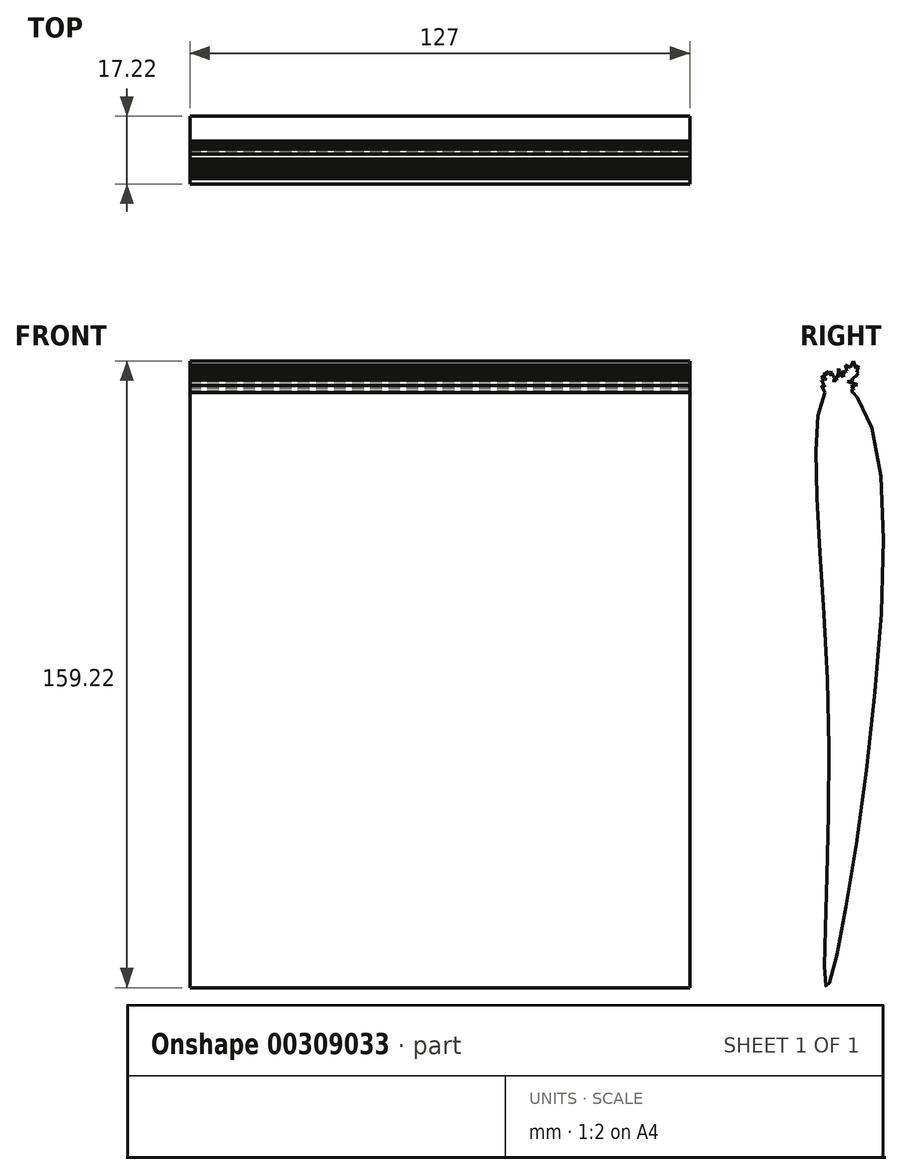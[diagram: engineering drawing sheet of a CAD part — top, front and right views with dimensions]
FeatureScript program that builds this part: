
annotation { "Feature Type Name" : "Feature", "Feature Type Description" : "" }
export const myFeature = defineFeature(function(context is Context, id is Id, definition is map)
    precondition{}
    {
        {
            var Q0;
            Q0=qCreatedBy(makeId("Right.planeOp"),FACE);
            var sketch = newSketch(context, id + "F0", { "sketchPlane" : qUnion([Q0])});
            skFitSpline(sketch, "E0", {"points": [v(-2.03, 75.34) * mm, v(9.75, 62.3) * mm, v(-2.03, -76.46) * mm, v(-2.03, -8.77) * mm, v(-2.03, 75.34) * mm]});
            skLineSegment(sketch, "E1", {"start": v(0.74, 76.19) * mm, "end": v(3, 80.27) * mm});
            skLineSegment(sketch, "E2", {"start": v(3, 80.27) * mm, "end": v(4.24, 79.58) * mm});
            skLineSegment(sketch, "E3", {"start": v(4.24, 79.58) * mm, "end": v(2.09, 75.7) * mm});
            skLineSegment(sketch, "E4", {"start": v(2.09, 75.7) * mm, "end": v(0.74, 76.19) * mm});
            skLineSegment(sketch, "E5", {"start": v(-0.38, 76.14) * mm, "end": v(-1.65, 78.86) * mm});
            skLineSegment(sketch, "E6", {"start": v(-1.65, 78.86) * mm, "end": v(-2.8, 78.32) * mm});
            skLineSegment(sketch, "E7", {"start": v(-2.8, 78.32) * mm, "end": v(-1.59, 75.67) * mm});
            skLineSegment(sketch, "E8", {"start": v(-1.59, 75.67) * mm, "end": v(-0.38, 76.14) * mm});
            skLineSegment(sketch, "E9", {"start": v(3.68, 74.6) * mm, "end": v(3.68, 76.14) * mm});
            skLineSegment(sketch, "E10", {"start": v(3.68, 76.14) * mm, "end": v(2.09, 75.7) * mm});
            skLineSegment(sketch, "E11", {"start": v(3.16, 77.64) * mm, "end": v(4.3, 77.02) * mm});
            skLineSegment(sketch, "E12", {"start": v(4.3, 77.02) * mm, "end": v(2.81, 77.02) * mm});
            skLineSegment(sketch, "E13", {"start": v(2.81, 77.02) * mm, "end": v(5.28, 76.24) * mm});
            skLineSegment(sketch, "E14", {"start": v(5.28, 76.24) * mm, "end": v(3.68, 75.7) * mm});
            skLineSegment(sketch, "E15", {"start": v(3.68, 75.7) * mm, "end": v(4.56, 75.21) * mm});
            skLineSegment(sketch, "E16", {"start": v(4.56, 75.21) * mm, "end": v(3.68, 74.6) * mm});
            skLineSegment(sketch, "E17", {"start": v(4.06, 79.26) * mm, "end": v(5.61, 77.98) * mm});
            skLineSegment(sketch, "E18", {"start": v(5.61, 77.98) * mm, "end": v(3.73, 77.33) * mm});
            skLineSegment(sketch, "E19", {"start": v(3.73, 77.33) * mm, "end": v(5.61, 79.02) * mm});
            skLineSegment(sketch, "E20", {"start": v(5.61, 79.02) * mm, "end": v(4.24, 79.58) * mm});
            skLineSegment(sketch, "E21", {"start": v(5.2, 79.19) * mm, "end": v(5.61, 80.99) * mm});
            skLineSegment(sketch, "E22", {"start": v(5.61, 80.99) * mm, "end": v(4.24, 79.58) * mm});
            skLineSegment(sketch, "E23", {"start": v(4.93, 80.29) * mm, "end": v(4.24, 82.18) * mm});
            skLineSegment(sketch, "E24", {"start": v(4.24, 82.18) * mm, "end": v(3.53, 80.45) * mm});
            skLineSegment(sketch, "E25", {"start": v(3.53, 80.45) * mm, "end": v(2.25, 81.17) * mm});
            skLineSegment(sketch, "E26", {"start": v(2.25, 81.17) * mm, "end": v(2.62, 79.58) * mm});
            skLineSegment(sketch, "E27", {"start": v(2.62, 79.58) * mm, "end": v(0.99, 79.2) * mm});
            skLineSegment(sketch, "E28", {"start": v(0.99, 79.2) * mm, "end": v(2.07, 78.6) * mm});
            skLineSegment(sketch, "E29", {"start": v(2.07, 78.6) * mm, "end": v(0.38, 78.02) * mm});
            skLineSegment(sketch, "E30", {"start": v(0.38, 78.02) * mm, "end": v(0.42, 80.28) * mm});
            skLineSegment(sketch, "E31", {"start": v(0.42, 80.28) * mm, "end": v(1.1, 78.27) * mm});
            skLineSegment(sketch, "E32", {"start": v(1.1, 78.27) * mm, "end": v(2.07, 78.6) * mm});
            skLineSegment(sketch, "E33", {"start": v(0.38, 78.02) * mm, "end": v(-0.23, 78.27) * mm});
            skLineSegment(sketch, "E34", {"start": v(-0.23, 78.27) * mm, "end": v(0.14, 77.19) * mm});
            skLineSegment(sketch, "E35", {"start": v(0.14, 77.19) * mm, "end": v(-0.43, 77.42) * mm});
            skLineSegment(sketch, "E36", {"start": v(-0.43, 77.42) * mm, "end": v(-0.69, 76.8) * mm});
            skLineSegment(sketch, "E37", {"start": v(-0.69, 76.8) * mm, "end": v(-0.58, 78.35) * mm});
            skLineSegment(sketch, "E38", {"start": v(-0.58, 78.35) * mm, "end": v(-1.44, 78.41) * mm});
            skLineSegment(sketch, "E39", {"start": v(-1.44, 78.41) * mm, "end": v(-1.44, 79.58) * mm});
            skLineSegment(sketch, "E40", {"start": v(-1.44, 79.58) * mm, "end": v(-1.84, 78.86) * mm});
            skLineSegment(sketch, "E41", {"start": v(-1.84, 78.86) * mm, "end": v(-2.58, 79.58) * mm});
            skLineSegment(sketch, "E42", {"start": v(-2.58, 79.58) * mm, "end": v(-2.15, 78.32) * mm});
            skLineSegment(sketch, "E43", {"start": v(-2.15, 78.32) * mm, "end": v(-3.46, 78.86) * mm});
            skLineSegment(sketch, "E44", {"start": v(-3.46, 78.86) * mm, "end": v(-2.33, 78.86) * mm});
            skLineSegment(sketch, "E45", {"start": v(-2.33, 78.86) * mm, "end": v(-3.96, 78.02) * mm});
            skLineSegment(sketch, "E46", {"start": v(-3.96, 78.02) * mm, "end": v(-2.67, 78.02) * mm});
            skLineSegment(sketch, "E47", {"start": v(-2.67, 78.02) * mm, "end": v(-3.4, 76.68) * mm});
            skLineSegment(sketch, "E48", {"start": v(-3.4, 76.68) * mm, "end": v(-2.2, 77.24) * mm});
            skPoint(sketch, "E48.endSnap0", {"position": v(-2.2, 77) * mm});
            skLineSegment(sketch, "E49", {"start": v(-2.2, 77.24) * mm, "end": v(-2.8, 76.05) * mm});
            skLineSegment(sketch, "E50", {"start": v(-2.8, 76.05) * mm, "end": v(-1.59, 75.67) * mm});
            skLineSegment(sketch, "E51", {"start": v(-2.5, 74.85) * mm, "end": v(-3.39, 75.34) * mm});
            skPoint(sketch, "E51.startSnap0", {"position": v(-2.5, 76.65) * mm});
            skLineSegment(sketch, "E52", {"start": v(-3.39, 75.34) * mm, "end": v(-2.03, 76.05) * mm});
            skLineSegment(sketch, "E53", {"start": v(-3.04, 77.35) * mm, "end": v(-3.85, 77.35) * mm});
            skLineSegment(sketch, "E54", {"start": v(-3.85, 77.35) * mm, "end": v(-3, 75.54) * mm});
            skLineSegment(sketch, "E55", {"start": v(-3, 75.54) * mm, "end": v(-3.82, 75.98) * mm});
            skLineSegment(sketch, "E56", {"start": v(-3.82, 75.98) * mm, "end": v(-2.98, 74.17) * mm});
            skLineSegment(sketch, "E57", {"start": v(-2.98, 74.17) * mm, "end": v(-2.5, 74.85) * mm});
            skLineSegment(sketch, "E58", {"start": v(-1.01, 78.35) * mm, "end": v(-1.01, 79.15) * mm});
            skPoint(sketch, "E58.startSnap0", {"position": v(-1.01, 78.38) * mm});
            skPoint(sketch, "E58.endSnap0", {"position": v(0.4, 79.15) * mm});
            skLineSegment(sketch, "E59", {"start": v(-1.01, 79.15) * mm, "end": v(-1.44, 78.41) * mm});
            skLineSegment(sketch, "E60", {"start": v(4.56, 73.73) * mm, "end": v(5.43, 75.21) * mm});
            skLineSegment(sketch, "E61", {"start": v(5.43, 75.21) * mm, "end": v(4.12, 74.2) * mm});
            skPoint(sketch, "E61.endSnap0", {"position": v(4.12, 74.91) * mm});
            skLineSegment(sketch, "E62", {"start": v(4.12, 74.2) * mm, "end": v(5.28, 76.24) * mm});
            skLineSegment(sketch, "E63", {"start": v(5.43, 75.21) * mm, "end": v(5.28, 76.24) * mm});
            skLineSegment(sketch, "E64", {"start": v(5, 74.47) * mm, "end": v(5.43, 74.22) * mm});
            skLineSegment(sketch, "E65", {"start": v(5.43, 74.22) * mm, "end": v(5.28, 73.96) * mm});
            skLineSegment(sketch, "E66", {"start": v(5.28, 73.96) * mm, "end": v(5.28, 72.85) * mm});
            skLineSegment(sketch, "E67", {"start": v(5.28, 72.85) * mm, "end": v(5.43, 74.22) * mm});
            skLineSegment(sketch, "E68", {"start": v(5, 74.47) * mm, "end": v(5.43, 74.77) * mm});
            skLineSegment(sketch, "E69", {"start": v(5.43, 74.77) * mm, "end": v(5.43, 74.22) * mm});
            skLineSegment(sketch, "E70", {"start": v(5.43, 75.21) * mm, "end": v(6.01, 76.24) * mm});
            skLineSegment(sketch, "E71", {"start": v(6.01, 76.24) * mm, "end": v(5.28, 76.24) * mm});
            skLineSegment(sketch, "E72", {"start": v(5.43, 75.21) * mm, "end": v(6.04, 75.64) * mm});
            skLineSegment(sketch, "E73", {"start": v(6.04, 75.64) * mm, "end": v(5.73, 75.6) * mm});
            skPoint(sketch, "E73.endSnap0", {"position": v(5.73, 75.43) * mm});
            skLineSegment(sketch, "E74", {"start": v(5.73, 75.6) * mm, "end": v(5.43, 75.21) * mm});
            skLineSegment(sketch, "E75", {"start": v(5.28, 76.24) * mm, "end": v(5.02, 77.02) * mm});
            skPoint(sketch, "E75.endSnap0", {"position": v(3.55, 77.02) * mm});
            skLineSegment(sketch, "E76", {"start": v(5.02, 77.02) * mm, "end": v(4.33, 76.54) * mm});
            skLineSegment(sketch, "E77", {"start": v(4.33, 76.54) * mm, "end": v(4.57, 77.33) * mm});
            skLineSegment(sketch, "E78", {"start": v(4.57, 77.33) * mm, "end": v(4.3, 77.02) * mm});
            skLineSegment(sketch, "E79", {"start": v(6.01, 76.24) * mm, "end": v(5.73, 76.64) * mm});
            skLineSegment(sketch, "E80", {"start": v(5.73, 76.64) * mm, "end": v(5.28, 76.24) * mm});
            skLineSegment(sketch, "E81", {"start": v(5.15, 76.63) * mm, "end": v(5.28, 76.86) * mm});
            skLineSegment(sketch, "E82", {"start": v(5.28, 76.86) * mm, "end": v(5.28, 76.24) * mm});
            skLineSegment(sketch, "E83", {"start": v(4.67, 76.78) * mm, "end": v(4.64, 77.02) * mm});
            skLineSegment(sketch, "E84", {"start": v(4.64, 77.02) * mm, "end": v(4.3, 77.02) * mm});
            skLineSegment(sketch, "E85", {"start": v(5.87, 76.44) * mm, "end": v(5.87, 77.02) * mm});
            skLineSegment(sketch, "E86", {"start": v(5.87, 77.02) * mm, "end": v(5.28, 76.5) * mm});
            skLineSegment(sketch, "E87", {"start": v(5.28, 76.5) * mm, "end": v(5.44, 77.02) * mm});
            skLineSegment(sketch, "E88", {"start": v(5.44, 77.02) * mm, "end": v(5.28, 76.86) * mm});
            skLineSegment(sketch, "E89", {"start": v(5.02, 77.02) * mm, "end": v(5.28, 77.25) * mm});
            skLineSegment(sketch, "E90", {"start": v(5.28, 77.25) * mm, "end": v(5.28, 76.86) * mm});
            skLineSegment(sketch, "E91", {"start": v(5.02, 77.02) * mm, "end": v(4.91, 77.33) * mm});
            skLineSegment(sketch, "E92", {"start": v(4.91, 77.33) * mm, "end": v(4.64, 77.02) * mm});
            skLineSegment(sketch, "E93", {"start": v(3.73, 77.33) * mm, "end": v(4.3, 77.41) * mm});
            skLineSegment(sketch, "E94", {"start": v(4.3, 77.41) * mm, "end": v(4.3, 77.02) * mm});
            skLineSegment(sketch, "E95", {"start": v(5.61, 77.98) * mm, "end": v(5.73, 78.37) * mm});
            skLineSegment(sketch, "E96", {"start": v(5.73, 78.37) * mm, "end": v(5.49, 78.09) * mm});
            skLineSegment(sketch, "E97", {"start": v(5.49, 78.09) * mm, "end": v(5.45, 78.6) * mm});
            skLineSegment(sketch, "E98", {"start": v(5.45, 78.6) * mm, "end": v(5.17, 78.35) * mm});
            skLineSegment(sketch, "E99", {"start": v(5.17, 78.35) * mm, "end": v(5.61, 79.02) * mm});
            skLineSegment(sketch, "E100", {"start": v(3.24, 77.37) * mm, "end": v(4.91, 77.33) * mm});
            skPoint(sketch, "E100.startSnap0", {"position": v(4.01, 77.37) * mm});
            skLineSegment(sketch, "E101", {"start": v(4.91, 77.33) * mm, "end": v(5.61, 77.98) * mm});
            skLineSegment(sketch, "E102", {"start": v(5.61, 79.02) * mm, "end": v(5.73, 79.88) * mm});
            skLineSegment(sketch, "E103", {"start": v(5.73, 79.88) * mm, "end": v(5.2, 79.19) * mm});
            skLineSegment(sketch, "E104", {"start": v(5.47, 79.54) * mm, "end": v(5.64, 80.29) * mm});
            skLineSegment(sketch, "E105", {"start": v(5.64, 80.29) * mm, "end": v(5.4, 80) * mm});
            skPoint(sketch, "E105.endSnap0", {"position": v(5.4, 80.09) * mm});
            skLineSegment(sketch, "E106", {"start": v(5.4, 80) * mm, "end": v(5.2, 79.19) * mm});
            skLineSegment(sketch, "E107", {"start": v(4.67, 80.98) * mm, "end": v(5.02, 81.43) * mm});
            skLineSegment(sketch, "E108", {"start": v(5.02, 81.43) * mm, "end": v(4.93, 80.29) * mm});
            skLineSegment(sketch, "E109", {"start": v(4.99, 80.82) * mm, "end": v(5.28, 80.82) * mm});
            skLineSegment(sketch, "E110", {"start": v(5.28, 80.82) * mm, "end": v(5.3, 80.66) * mm});
            skSolve(sketch);
        }
        {
            var Q0;
            {var subQ6=sQuery(id+"F0.wireOp",EDGE,"E8");Q0=makeQuery(id+"F0.imprint","IMPRINT",FACE,{"disambiguationData":[TD([[makeQuery(id+"F0.imprint","IMPRINT",EDGE,{"derivedFrom":subQ6}),-1.0]])]});}
            var Q1;
            {var subQ3=sQuery(id+"F0.wireOp",EDGE,"E6");var subQ15=sQuery(id+"F0.wireOp",EDGE,"E5");var subQ17=makeQuery(id+"F0.imprint","INTERSECT",VERTEX,{"derivedFrom":[subQ15,subQ3]});Q1=makeQuery(id+"F0.imprint","IMPRINT",FACE,{"disambiguationData":[TD([[makeQuery(id+"F0.imprint","IMPRINT",EDGE,{"disambiguationData":[TD([[subQ17,-1.0]])],"derivedFrom":subQ3}),1.0]])]});}
            var Q2;
            {var subQ2=sQuery(id+"F0.wireOp",EDGE,"E2");Q2=makeQuery(id+"F0.imprint","IMPRINT",FACE,{"disambiguationData":[TD([[makeQuery(id+"F0.imprint","IMPRINT",EDGE,{"derivedFrom":subQ2}),1.0]])]});}
            var Q3;
            {var subQ0=sQuery(id+"F0.wireOp",EDGE,"E10");Q3=makeQuery(id+"F0.imprint","IMPRINT",FACE,{"disambiguationData":[TD([[makeQuery(id+"F0.imprint","IMPRINT",EDGE,{"derivedFrom":subQ0}),-1.0]])]});}
            var Q4;
            {var subQ0=sQuery(id+"F0.wireOp",EDGE,"E2");Q4=makeQuery(id+"F0.imprint","IMPRINT",FACE,{"disambiguationData":[TD([[makeQuery(id+"F0.imprint","IMPRINT",EDGE,{"derivedFrom":subQ0}),-1.0]])]});}
            var Q5;
            {var subQ0=sQuery(id+"F0.wireOp",EDGE,"E10");Q5=makeQuery(id+"F0.imprint","IMPRINT",FACE,{"disambiguationData":[TD([[makeQuery(id+"F0.imprint","IMPRINT",EDGE,{"derivedFrom":subQ0}),1.0]])]});}
            var Q6;
            Q6=makeQuery(id+"F0.imprint","IMPRINT",FACE,{"disambiguationData":[TD([[makeQuery(id+"F0.imprint","IMPRINT",EDGE,{"derivedFrom":sQuery(id+"F0.wireOp",EDGE,"E29")}),1.0]])]});
            var Q7;
            {var subQ0=sQuery(id+"F0.wireOp",EDGE,"E11");var subQ1=sQuery(id+"F0.wireOp",EDGE,"E3");var subQ2=makeQuery(id+"F0.imprint","INTERSECT",VERTEX,{"derivedFrom":[subQ1,subQ0]});Q7=makeQuery(id+"F0.imprint","IMPRINT",FACE,{"disambiguationData":[TD([[makeQuery(id+"F0.imprint","IMPRINT",EDGE,{"disambiguationData":[TD([[subQ2,1.0]])],"derivedFrom":subQ1}),1.0]])]});}
            var Q8;
            {var subQ0=sQuery(id+"F0.wireOp",EDGE,"E18");Q8=makeQuery(id+"F0.imprint","IMPRINT",FACE,{"disambiguationData":[TD([[makeQuery(id+"F0.imprint","IMPRINT",EDGE,{"derivedFrom":subQ0}),-1.0]])]});}
            var Q9;
            {var subQ2=sQuery(id+"F0.wireOp",EDGE,"E15");Q9=makeQuery(id+"F0.imprint","IMPRINT",FACE,{"disambiguationData":[TD([[makeQuery(id+"F0.imprint","IMPRINT",EDGE,{"derivedFrom":subQ2}),-1.0]])]});}
            var Q10;
            Q10=makeQuery(id+"F0.imprint","IMPRINT",FACE,{"disambiguationData":[TD([[makeQuery(id+"F0.imprint","IMPRINT",EDGE,{"derivedFrom":sQuery(id+"F0.wireOp",EDGE,"E29")}),-1.0]])]});
            var Q11;
            {var subQ0=sQuery(id+"F0.wireOp",EDGE,"E4");var subQ1=sQuery(id+"F0.wireOp",EDGE,"E0");var subQ3=makeQuery(id+"F0.imprint","INTERSECT",VERTEX,{"derivedFrom":[subQ1,subQ0]});Q11=makeQuery(id+"F0.imprint","IMPRINT",FACE,{"disambiguationData":[TD([[makeQuery(id+"F0.imprint","IMPRINT",EDGE,{"disambiguationData":[TD([[subQ3,-1.0]])],"derivedFrom":subQ1}),-1.0]])]});}
            var Q12;
            {var subQ0=sQuery(id+"F0.wireOp",EDGE,"E27");Q12=makeQuery(id+"F0.imprint","IMPRINT",FACE,{"disambiguationData":[TD([[makeQuery(id+"F0.imprint","IMPRINT",EDGE,{"derivedFrom":subQ0}),1.0]])]});}
            var Q13;
            {var subQ0=sQuery(id+"F0.wireOp",EDGE,"E8");Q13=makeQuery(id+"F0.imprint","IMPRINT",FACE,{"disambiguationData":[TD([[makeQuery(id+"F0.imprint","IMPRINT",EDGE,{"derivedFrom":subQ0}),1.0]])]});}
            var Q14;
            {var subQ1=sQuery(id+"F0.wireOp",EDGE,"E51");Q14=makeQuery(id+"F0.imprint","IMPRINT",FACE,{"disambiguationData":[TD([[makeQuery(id+"F0.imprint","IMPRINT",EDGE,{"derivedFrom":subQ1}),1.0]])]});}
            var Q15;
            {var subQ8=sQuery(id+"F0.wireOp",EDGE,"E53");Q15=makeQuery(id+"F0.imprint","IMPRINT",FACE,{"disambiguationData":[TD([[makeQuery(id+"F0.imprint","IMPRINT",EDGE,{"derivedFrom":subQ8}),1.0]])]});}
            var Q16;
            {var subQ3=sQuery(id+"F0.wireOp",EDGE,"E12");Q16=makeQuery(id+"F0.imprint","IMPRINT",FACE,{"disambiguationData":[TD([[makeQuery(id+"F0.imprint","IMPRINT",EDGE,{"derivedFrom":subQ3}),-1.0]])]});}
            var Q17;
            {var subQ3=sQuery(id+"F0.wireOp",EDGE,"E17");var subQ6=sQuery(id+"F0.wireOp",EDGE,"E3");var subQ7=makeQuery(id+"F0.imprint","INTERSECT",VERTEX,{"derivedFrom":[subQ6,subQ3]});Q17=makeQuery(id+"F0.imprint","IMPRINT",FACE,{"disambiguationData":[TD([[makeQuery(id+"F0.imprint","IMPRINT",EDGE,{"disambiguationData":[TD([[subQ7,-1.0]])],"derivedFrom":subQ3}),1.0]])]});}
            var Q18;
            {var subQ3=sQuery(id+"F0.wireOp",EDGE,"E21");Q18=makeQuery(id+"F0.imprint","IMPRINT",FACE,{"disambiguationData":[TD([[makeQuery(id+"F0.imprint","IMPRINT",EDGE,{"derivedFrom":subQ3}),1.0]])]});}
            var Q19;
            {var subQ0=sQuery(id+"F0.wireOp",EDGE,"E47");var subQ3=sQuery(id+"F0.wireOp",EDGE,"E48");var subQ5=makeQuery(id+"F0.imprint","INTERSECT",VERTEX,{"derivedFrom":[subQ0,subQ3]});Q19=makeQuery(id+"F0.imprint","IMPRINT",FACE,{"disambiguationData":[TD([[makeQuery(id+"F0.imprint","IMPRINT",EDGE,{"disambiguationData":[TD([[subQ5,1.0]])],"derivedFrom":subQ0}),1.0]])]});}
            var Q20;
            {var subQ1=sQuery(id+"F0.wireOp",EDGE,"E51");Q20=makeQuery(id+"F0.imprint","IMPRINT",FACE,{"disambiguationData":[TD([[makeQuery(id+"F0.imprint","IMPRINT",EDGE,{"derivedFrom":subQ1}),-1.0]])]});}
            var Q21;
            {var subQ0=sQuery(id+"F0.wireOp",EDGE,"E50");var subQ3=sQuery(id+"F0.wireOp",EDGE,"E49");var subQ5=makeQuery(id+"F0.imprint","INTERSECT",VERTEX,{"derivedFrom":[subQ3,subQ0]});Q21=makeQuery(id+"F0.imprint","IMPRINT",FACE,{"disambiguationData":[TD([[makeQuery(id+"F0.imprint","IMPRINT",EDGE,{"disambiguationData":[TD([[subQ5,1.0]])],"derivedFrom":subQ3}),1.0]])]});}
            var Q22;
            {var subQ0=sQuery(id+"F0.wireOp",EDGE,"E57");Q22=makeQuery(id+"F0.imprint","IMPRINT",FACE,{"disambiguationData":[TD([[makeQuery(id+"F0.imprint","IMPRINT",EDGE,{"derivedFrom":subQ0}),1.0]])]});}
            var Q23;
            {var subQ0=sQuery(id+"F0.wireOp",EDGE,"E37");Q23=makeQuery(id+"F0.imprint","IMPRINT",FACE,{"disambiguationData":[TD([[makeQuery(id+"F0.imprint","IMPRINT",EDGE,{"derivedFrom":subQ0}),1.0]])]});}
            var Q24;
            {var subQ0=sQuery(id+"F0.wireOp",EDGE,"E44");Q24=makeQuery(id+"F0.imprint","IMPRINT",FACE,{"disambiguationData":[TD([[makeQuery(id+"F0.imprint","IMPRINT",EDGE,{"derivedFrom":subQ0}),-1.0]])]});}
            var Q25;
            {var subQ0=sQuery(id+"F0.wireOp",EDGE,"E48");var subQ1=sQuery(id+"F0.wireOp",EDGE,"E7");var subQ2=makeQuery(id+"F0.imprint","INTERSECT",VERTEX,{"derivedFrom":[subQ1,subQ0]});Q25=makeQuery(id+"F0.imprint","IMPRINT",FACE,{"disambiguationData":[TD([[makeQuery(id+"F0.imprint","IMPRINT",EDGE,{"disambiguationData":[TD([[subQ2,-1.0]])],"derivedFrom":subQ1}),1.0]])]});}
            var Q26;
            {var subQ0=sQuery(id+"F0.wireOp",EDGE,"E46");Q26=makeQuery(id+"F0.imprint","IMPRINT",FACE,{"disambiguationData":[TD([[makeQuery(id+"F0.imprint","IMPRINT",EDGE,{"derivedFrom":subQ0}),1.0]])]});}
            var Q27;
            {var subQ0=sQuery(id+"F0.wireOp",EDGE,"E42");var subQ1=sQuery(id+"F0.wireOp",EDGE,"E6");var subQ2=makeQuery(id+"F0.imprint","INTERSECT",VERTEX,{"derivedFrom":[subQ1,subQ0]});Q27=makeQuery(id+"F0.imprint","IMPRINT",FACE,{"disambiguationData":[TD([[makeQuery(id+"F0.imprint","IMPRINT",EDGE,{"disambiguationData":[TD([[subQ2,-1.0]])],"derivedFrom":subQ1}),-1.0]])]});}
            var Q28;
            {var subQ0=sQuery(id+"F0.wireOp",EDGE,"E42");var subQ1=sQuery(id+"F0.wireOp",EDGE,"E6");var subQ2=makeQuery(id+"F0.imprint","INTERSECT",VERTEX,{"derivedFrom":[subQ1,subQ0]});Q28=makeQuery(id+"F0.imprint","IMPRINT",FACE,{"disambiguationData":[TD([[makeQuery(id+"F0.imprint","IMPRINT",EDGE,{"disambiguationData":[TD([[subQ2,-1.0]])],"derivedFrom":subQ1}),1.0]])]});}
            var Q29;
            {var subQ0=sQuery(id+"F0.wireOp",EDGE,"E39");Q29=makeQuery(id+"F0.imprint","IMPRINT",FACE,{"disambiguationData":[TD([[makeQuery(id+"F0.imprint","IMPRINT",EDGE,{"derivedFrom":subQ0}),1.0]])]});}
            var Q30;
            {var subQ0=sQuery(id+"F0.wireOp",EDGE,"E59");Q30=makeQuery(id+"F0.imprint","IMPRINT",FACE,{"disambiguationData":[TD([[makeQuery(id+"F0.imprint","IMPRINT",EDGE,{"derivedFrom":subQ0}),1.0]])]});}
            extrude(context, id + "F1", {"entities" : qUnion([Q0, Q1, Q2, Q3, Q4, Q5, Q6, Q7, Q8, Q9, Q10, Q11, Q12, Q13, Q14, Q15, Q16, Q17, Q18, Q19, Q20, Q21, Q22, Q23, Q24, Q25, Q26, Q27, Q28, Q29, Q30]), "endBound" : BoundingType.SYMMETRIC, "depth" : 127 * mm});
        }
    });
